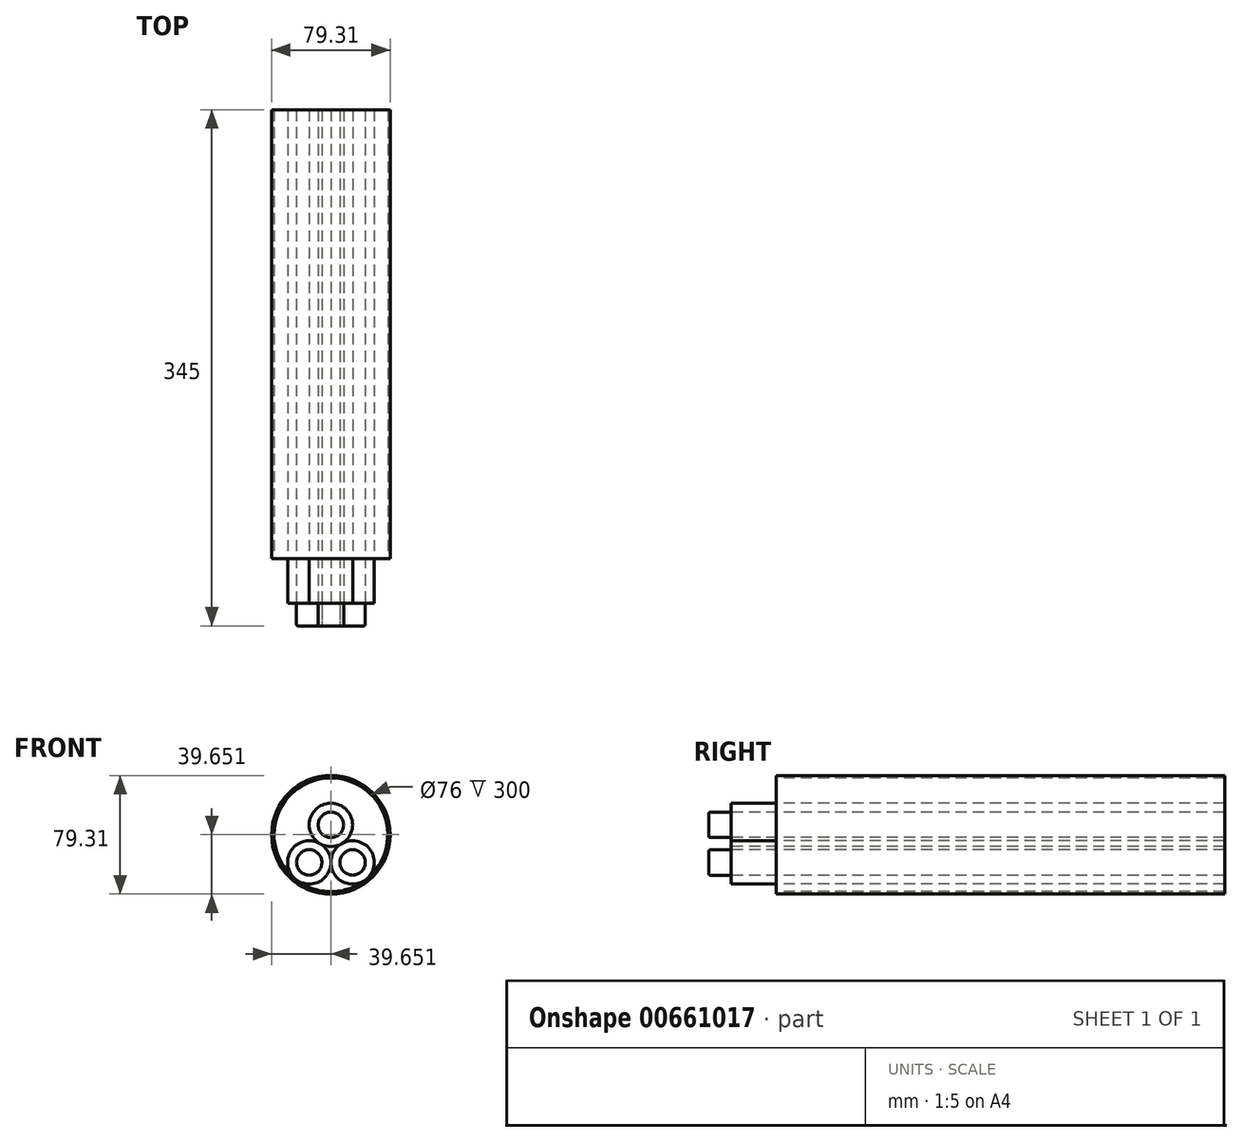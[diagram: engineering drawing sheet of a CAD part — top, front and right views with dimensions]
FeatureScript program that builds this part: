
annotation { "Feature Type Name" : "Feature", "Feature Type Description" : "" }
export const myFeature = defineFeature(function(context is Context, id is Id, definition is map)
    precondition{}
    {
        {
            var Q0;
            Q0=qCreatedBy(makeId("Front.planeOp"),FACE);
            var sketch = newSketch(context, id + "F0", { "sketchPlane" : qUnion([Q0])});
            skCircle(sketch, "E0", {"center": v(-58.59, 37.11) * mm, "radius": 38 * mm});
            skCircle(sketch, "E1", {"center": v(-73.09, 18.62) * mm, "radius": 14.5 * mm});
            skCircle(sketch, "E2", {"center": v(-44.09, 18.62) * mm, "radius": 14.5 * mm});
            skCircle(sketch, "E3", {"center": v(-58.59, 43.73) * mm, "radius": 14.5 * mm});
            skCircle(sketch, "E4", {"center": v(-58.59, 43.73) * mm, "radius": 8.5 * mm});
            skCircle(sketch, "E5", {"center": v(-73.09, 18.62) * mm, "radius": 8.5 * mm});
            skCircle(sketch, "E6", {"center": v(-44.09, 18.62) * mm, "radius": 8.5 * mm});
            skCircle(sketch, "E7", {"center": v(-58.59, 37.11) * mm, "radius": 39.66 * mm});
            skSolve(sketch);
        }
        {
            var Q0;
            Q0=makeQuery(id+"F0.imprint","IMPRINT",FACE,{"disambiguationData":[TD([[makeQuery(id+"F0.imprint","IMPRINT",EDGE,{"derivedFrom":sQuery(id+"F0.wireOp",EDGE,"E7")}),1.0]])]});
            extrude(context, id + "F1", {"entities" : qUnion([Q0]), "oppositeDirection" : true, "depth" : 300 * mm, "offsetDistance" : 25 * mm});
        }
        {
            var Q0;
            Q0=makeQuery(id+"F0.imprint","IMPRINT",FACE,{"disambiguationData":[TD([[makeQuery(id+"F0.imprint","IMPRINT",EDGE,{"derivedFrom":sQuery(id+"F0.wireOp",EDGE,"E4")}),-1.0]])]});
            var Q1;
            Q1=makeQuery(id+"F0.imprint","IMPRINT",FACE,{"disambiguationData":[TD([[makeQuery(id+"F0.imprint","IMPRINT",EDGE,{"derivedFrom":sQuery(id+"F0.wireOp",EDGE,"E5")}),-1.0]])]});
            var Q2;
            Q2=makeQuery(id+"F0.imprint","IMPRINT",FACE,{"disambiguationData":[TD([[makeQuery(id+"F0.imprint","IMPRINT",EDGE,{"derivedFrom":sQuery(id+"F0.wireOp",EDGE,"E6")}),-1.0]])]});
            extrude(context, id + "F2", {"entities" : qUnion([Q0, Q1, Q2]), "operationType" : NewBodyOperationType.ADD, "oppositeDirection" : true, "depth" : 300 * mm, "offsetDistance" : 25 * mm, "hasSecondDirection" : true, "secondDirectionOppositeDirection" : false, "secondDirectionDepth" : 30 * mm});
        }
        {
            var Q0;
            Q0=makeQuery(id+"F0.imprint","IMPRINT",FACE,{"disambiguationData":[TD([[makeQuery(id+"F0.imprint","IMPRINT",EDGE,{"derivedFrom":sQuery(id+"F0.wireOp",EDGE,"E4")}),1.0]])]});
            var Q1;
            Q1=makeQuery(id+"F0.imprint","IMPRINT",FACE,{"disambiguationData":[TD([[makeQuery(id+"F0.imprint","IMPRINT",EDGE,{"derivedFrom":sQuery(id+"F0.wireOp",EDGE,"E5")}),1.0]])]});
            var Q2;
            Q2=makeQuery(id+"F0.imprint","IMPRINT",FACE,{"disambiguationData":[TD([[makeQuery(id+"F0.imprint","IMPRINT",EDGE,{"derivedFrom":sQuery(id+"F0.wireOp",EDGE,"E6")}),1.0]])]});
            extrude(context, id + "F3", {"entities" : qUnion([Q0, Q1, Q2]), "oppositeDirection" : true, "depth" : 300 * mm, "offsetDistance" : 25 * mm, "hasSecondDirection" : true, "secondDirectionOppositeDirection" : false, "secondDirectionDepth" : 45 * mm});
        }
        {
            var Q0;
            Q0=makeQuery(id+"F3.opExtrude","CAP_EDGE",EDGE,{"disambiguationData":[OSD([sQuery(id+"F0.wireOp",EDGE,"E4")])],"isStart":true});
            var Q1;
            Q1=makeQuery(id+"F3.opExtrude","CAP_EDGE",EDGE,{"disambiguationData":[OSD([sQuery(id+"F0.wireOp",EDGE,"E5")])],"isStart":true});
            var Q2;
            Q2=makeQuery(id+"F3.opExtrude","CAP_EDGE",EDGE,{"disambiguationData":[OSD([sQuery(id+"F0.wireOp",EDGE,"E6")])],"isStart":true});
            fillet(context, id + "F4", {"entities" : qUnion([Q0, Q1, Q2]), "radius" : 1 * mm, "tangentPropagation" : true, "allowEdgeOverflow" : false});
        }
    });
